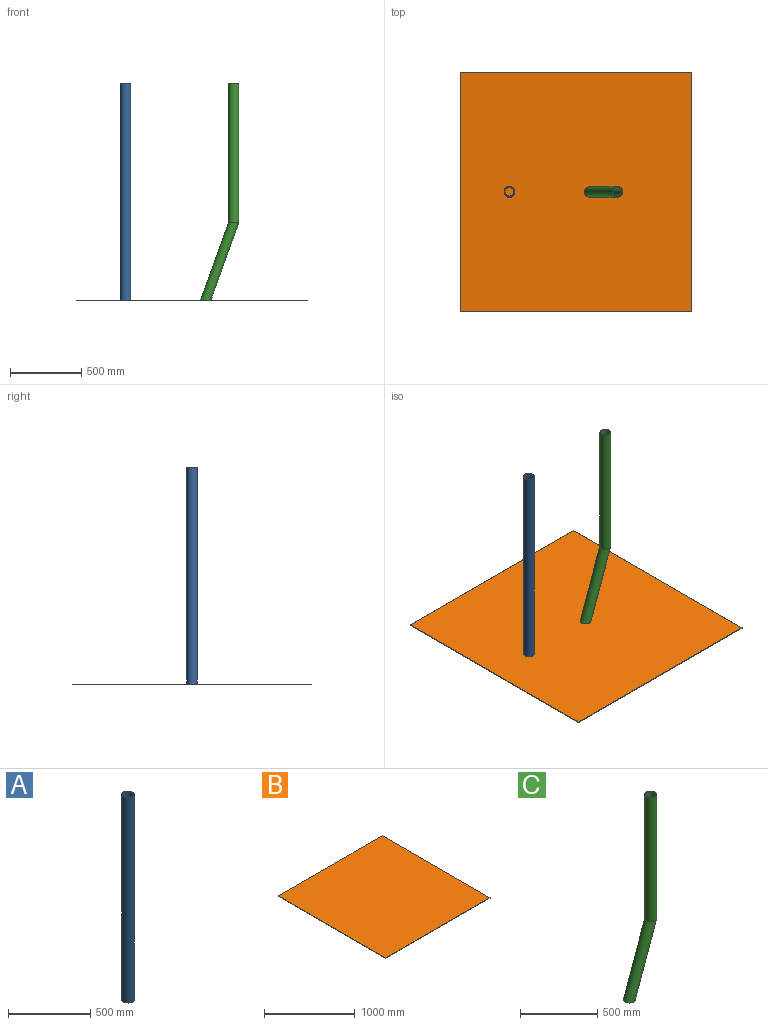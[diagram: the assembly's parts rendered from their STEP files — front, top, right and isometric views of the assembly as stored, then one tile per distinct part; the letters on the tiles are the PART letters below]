
ASSEMBLY  parts=3 mates=2
PART A: 4 faces, bbox 76.2x76.2x1524 mm
  f0: cylinder r=31.75mm len=1524mm, axis (0,0,-1), area 304024.5mm2, adj f2,f3
  f1: cylinder r=38.1mm len=1524mm, axis (0,0,-1), area 364829.4mm2, adj f2,f3
  f2: plane 76.2x76.2mm, normal (0,0,1), area 1393.4mm2, adj f0,f1
  f3: plane 76.2x76.2mm, normal (0,0,-1), area 1393.4mm2, adj f0,f1
PART B: 6 faces, bbox 1625.6x1676.4x4.8 mm
  f0: plane 1625.6x4.76mm, normal (0,-1,0), area 7741.9mm2, adj f1,f3,f4,f5
  f1: plane 1676.4x4.76mm, normal (1,0,0), area 7983.9mm2, adj f0,f2,f4,f5
  f2: plane 1625.6x4.76mm, normal (0,1,0), area 7741.9mm2, adj f1,f3,f4,f5
  f3: plane 1676.4x4.76mm, normal (-1,0,0), area 7983.9mm2, adj f0,f2,f4,f5
  f4: plane 1676.4x1625.6mm, normal (0,0,1), area 2725155.8mm2, adj f0,f1,f2,f3
  f5: plane 1676.4x1625.6mm, normal (0,0,-1), area 2725155.8mm2, adj f0,f1,f2,f3
PART C: 6 faces, bbox 272.3x152.4x1524 mm
  f0: cylinder r=31.75mm len=980.44mm, axis (0,0,1), area 195589.1mm2, adj f1,f2
  f1: bspline ~543.56x259.59mm, area 112104.7mm2, adj f0,f3
  f2: plane 76.2x76.2mm, normal (0,0,1), area 1393.4mm2, adj f0,f4
  f3: plane 76.2x76.2mm, normal (0,0,-1), area 1393.4mm2, adj f1,f5
  f4: cylinder r=38.1mm len=980.44mm, axis (0,0,1), area 234706.9mm2, adj f2,f5
  f5: bspline ~543.56x272.29mm, area 134525.6mm2, adj f3,f4
PLACE A t=(-87.31,0,0)mm
PLACE B at identity
PLACE C t=(-311.15,0,0)mm
MATE fastened A.f1 <-> B.f4  axis (0,0,-1) through (-468.31,0,4.76)mm
MATE fastened C.f3 <-> B.f4  axis (0,0,-1) through (95.25,0,4.76)mm
